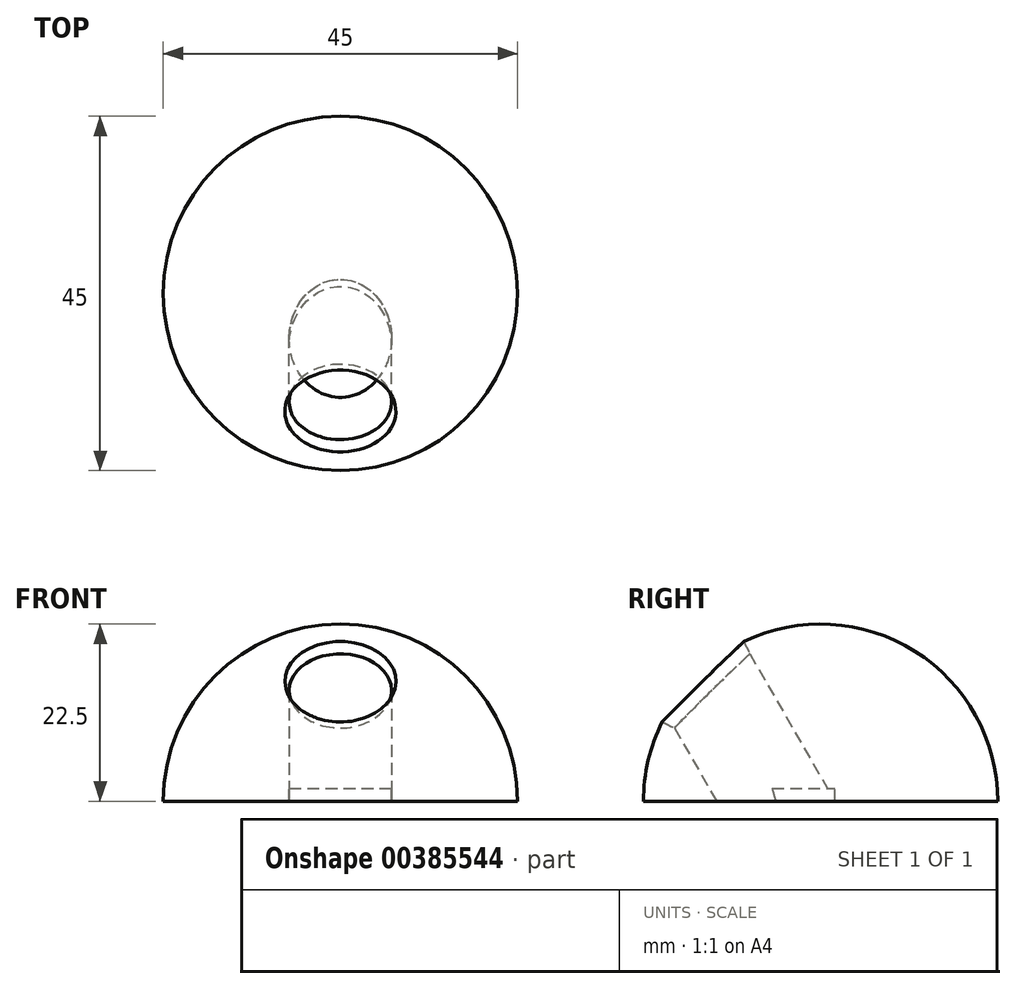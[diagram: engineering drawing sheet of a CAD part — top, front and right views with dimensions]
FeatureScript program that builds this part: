
annotation { "Feature Type Name" : "Feature", "Feature Type Description" : "" }
export const myFeature = defineFeature(function(context is Context, id is Id, definition is map)
    precondition{}
    {
        {
            var Q0;
            Q0=qCreatedBy(makeId("Top.planeOp"),FACE);
            var sketch = newSketch(context, id + "F0", { "sketchPlane" : qUnion([Q0])});
            skEllipse(sketch, "E0", {"center": v(0, 22.5) * mm, "majorRadius": 22.5 * mm, "minorRadius": 22.5 * mm, "majorAxis": v(0, -1)});
            skSolve(sketch);
        }
        {
            var Q0;
            Q0 = qSketchRegion(id + "F0", true);
            var sketch = newSketch(context, id + "F1", { "sketchPlane" : qUnion([Q0])});
            skLineSegment(sketch, "E1", {"start": v(0, 0) * mm, "end": v(0, 276.12) * mm});
            skSolve(sketch);
        }
        {
            var Q0;
            {var subQ0=sQuery(id+"F1.wireOp",EDGE,"E1");var subQ1=makeQuery(id+"F0.imprint","IMPRINT",EDGE,{"derivedFrom":sQuery(id+"F0.wireOp",EDGE,"E0")});var subQ2=makeQuery(id+"F1.imprint","INTERSECT",VERTEX,{"disambiguationData":[OD(0.0)],"derivedFrom":[subQ1,subQ0]});Q0=makeQuery(id+"F1.imprint","IMPRINT",FACE,{"disambiguationData":[TD([[makeQuery(id+"F1.imprint","IMPRINT",EDGE,{"disambiguationData":[TD([[subQ2,-1.0]])],"derivedFrom":subQ0}),1.0]])]});}
            var Q1;
            Q1=sQuery(id+"F1.wireOp",EDGE,"E1");
            revolve(context, id + "F2", {"entities" : qUnion([Q0]), "axis" : qUnion([Q1]), "revolveType" : RevolveType.ONE_DIRECTION, "angle" : 180 * degree});
        }
        {
            var Q0;
            Q0=qCreatedBy(makeId("Top.planeOp"),FACE);
            var sketch = newSketch(context, id + "F3", { "sketchPlane" : qUnion([Q0])});
            skCircle(sketch, "E2", {"center": v(0, 0) * mm, "radius": 6.5 * mm});
            skLineSegment(sketch, "E3", {"start": v(0, 0) * mm, "end": v(50.7, 0) * mm});
            skSolve(sketch);
        }
        {
            var Q0;
            Q0=makeQuery(id+"F3.imprint","IMPRINT",FACE,{"disambiguationData":[TD([[makeQuery(id+"F3.imprint","IMPRINT",EDGE,{"derivedFrom":sQuery(id+"F3.wireOp",EDGE,"E2")}),1.0]])]});
            var Q1;
            Q1=sQuery(id+"F3.wireOp",EDGE,"E2");
            extrude(context, id + "F4", {"entities" : qUnion([Q0]), "surfaceEntities" : qUnion([Q1]), "depth" : 50 * mm});
        }
        {
            var Q0;
            Q0=makeQuery(id+"F4.opExtrude","SWEPT_BODY",BODY,{"disambiguationData":[OSD([sQuery(id+"F3.wireOp",EDGE,"E2")])]});
            var Q1;
            Q1=sQuery(id+"F3.wireOp",EDGE,"E3");
            transform(context, id + "F5", {"entities" : qUnion([Q0]), "transformType" : TransformType.ROTATION, "transformAxis" : qUnion([Q1]), "angle" : 30 * degree, "makeCopy" : false});
        }
        {
            var Q0;
            Q0=makeQuery(id+"F4.opExtrude","SWEPT_BODY",BODY,{"disambiguationData":[OSD([sQuery(id+"F3.wireOp",EDGE,"E2")])]});
            var Q1;
            Q1=sQuery(id+"F1.wireOp",EDGE,"E1");
            transform(context, id + "F6", {"entities" : qUnion([Q0]), "transformType" : TransformType.TRANSLATION_DISTANCE, "transformDirection" : qUnion([Q1]), "distance" : 16.8 * mm, "makeCopy" : false});
        }
        {
            var Q0;
            Q0=makeQuery(id+"F4.opExtrude","SWEPT_BODY",BODY,{"disambiguationData":[OSD([sQuery(id+"F3.wireOp",EDGE,"E2")])]});
            var Q1;
            Q1=makeQuery(id+"F4.opExtrude","SWEPT_FACE",FACE,{"disambiguationData":[OSD([sQuery(id+"F3.wireOp",EDGE,"E2")])]});
            transform(context, id + "F7", {"entities" : qUnion([Q0]), "transformType" : TransformType.TRANSLATION_DISTANCE, "transformDirection" : qUnion([Q1]), "distance" : 12.2 * mm, "makeCopy" : false});
        }
        {
            var Q0;
            Q0=makeQuery(id+"F4.opExtrude","SWEPT_BODY",BODY,{"disambiguationData":[OSD([sQuery(id+"F3.wireOp",EDGE,"E2")])]});
            var Q1;
            Q1=makeQuery(id+"F2.opRevolve","SWEPT_BODY",BODY,{"disambiguationData":[OSD([sQuery(id+"F0.wireOp",EDGE,"E0"),sQuery(id+"F1.wireOp",EDGE,"E1")])]});
            booleanBodies(context, id + "F8", {"operationType" : BooleanOperationType.SUBTRACTION, "tools" : qUnion([Q0]), "targets" : qUnion([Q1])});
        }
        {
            var Q0;
            Q0=makeQuery(id+"F2.opRevolve","CAP_FACE",FACE,{"disambiguationData":[OSD([sQuery(id+"F0.wireOp",EDGE,"E0"),sQuery(id+"F1.wireOp",EDGE,"E1")])],"isStart":false});
            var sketch = newSketch(context, id + "F9", { "sketchPlane" : qUnion([Q0])});
            skLineSegment(sketch, "E4.bottom", {"start": v(-3, -22) * mm, "end": v(3, -22) * mm});
            skLineSegment(sketch, "E4.top", {"start": v(-3, -47) * mm, "end": v(3, -47) * mm});
            skLineSegment(sketch, "E4.left", {"start": v(-3, -22) * mm, "end": v(-3, -47) * mm});
            skLineSegment(sketch, "E4.right", {"start": v(3, -22) * mm, "end": v(3, -47) * mm});
            skSolve(sketch);
        }
        {
            var Q0;
            {var subQ0=sQuery(id+"F0.wireOp",EDGE,"E0");var subQ1=makeQuery(id+"F2.opRevolve","CAP_EDGE",EDGE,{"disambiguationData":[OSD([subQ0])],"isStart":false});var subQ2=makeQuery(id+"F2.opRevolve","CAP_EDGE",EDGE,{"disambiguationData":[OSD([subQ0])],"isStart":true});var subQ3=makeQuery(id+"F9.imprint","INTERSECT",VERTEX,{"disambiguationData":[OD(1.0)],"derivedFrom":[subQ2,subQ1]});Q0=makeQuery(id+"F9.imprint","IMPRINT",FACE,{"disambiguationData":[TD([[makeQuery(id+"F9.imprint","IMPRINT",EDGE,{"disambiguationData":[TD([[subQ3,-1.0]])],"derivedFrom":subQ2}),-1.0]])]});}
            var Q1;
            {var subQ0=sQuery(id+"F9.wireOp",EDGE,"E4.bottom");Q1=makeQuery(id+"F9.imprint","IMPRINT",FACE,{"disambiguationData":[TD([[makeQuery(id+"F9.imprint","IMPRINT",EDGE,{"derivedFrom":subQ0}),-1.0]])]});}
            var Q2;
            {var subQ0=sQuery(id+"F9.wireOp",EDGE,"E4.bottom");Q2=makeQuery(id+"F9.imprint","IMPRINT",FACE,{"disambiguationData":[TD([[makeQuery(id+"F9.imprint","IMPRINT",EDGE,{"derivedFrom":subQ0}),1.0]])]});}
            extrude(context, id + "F10", {"entities" : qUnion([Q0, Q1, Q2]), "operationType" : NewBodyOperationType.REMOVE, "oppositeDirection" : true, "depth" : 1.6 * mm});
        }
        {
            var Q0;
            Q0=makeQuery(id+"F8.opBoolean","INTERSECT",EDGE,{"derivedFrom":[makeQuery(id+"F2.opRevolve","SWEPT_FACE",FACE,{"disambiguationData":[OSD([sQuery(id+"F0.wireOp",EDGE,"E0")])]}),makeQuery(id+"F4.opExtrude","SWEPT_FACE",FACE,{"disambiguationData":[OSD([sQuery(id+"F3.wireOp",EDGE,"E2")])]})]});
            chamfer(context, id + "F11", {"entities" : qUnion([Q0]), "chamferType" : ChamferType.TWO_OFFSETS, "width1" : 2 * mm, "oppositeDirection" : false, "width2" : 1 * mm});
        }
    });
